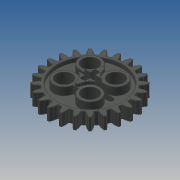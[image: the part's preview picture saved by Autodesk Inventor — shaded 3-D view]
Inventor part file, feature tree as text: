
AUTODESK INVENTOR PART (.ipt)
format: ipt  version: 2022.2 (Build 262287000, 287)  size: 1,320,448 bytes
history: native  units: in
note: dims shown in document units (in); Inventor stores cm internally (conversion verified against a paired STEP export)
features: extrude x5, fillet x2, sketch x1, pattern_circular x1
ambient origin geometry x8: Origin, YZ Plane, XZ Plane, XY Plane, X Axis, Y Axis, Z Axis, Center Point
bodies: Solid1 (feature_tree)
feature tree (9):
  sketch  "Sketch2"  dims[d0=0.189in d2=0.189in d3=0.315in d4=0.315in d5=0.7874in d6=0.8504in d7=0.0551in d8=0.0252in d10=0.9429in d11=1.0205in d12=0.13in d13=0.063in d14=0.063in d15=0.5039in d18=0.3445in d20=0.263in d21=0.0551in d22=0.0in d23=0.1496in d24=0.0in d25=0.2457in d26=0.0in d27=0.0008in d28=0.0008in d29=0.315in d30=0.0in d31=0.1496in d32=0.0in d34=0.0039in d35=9.4488in d36=360.0deg d38=0.0039in]
  extrude  "Extrusion1"  Depth=0.0039in
  extrude  "Extrusion2"  Depth=0.0039in
  extrude  "Extrusion3"  Depth=0.0039in
  extrude  "Extrusion4"  Depth=0.0039in
  extrude  "Extrusion5"  Depth=0.0039in
  fillet  "Fillet2"  Radius=0.0551in
  pattern_circular  "Circular Pattern1"  [2 undecoded]
  fillet  "Fillet3"  Radius=0.9429in
note: 2 required parameter values undecoded (feature->parameter linkage not recoverable at this tier; creation-order binding heuristic only, values carry confidence <= 0.55)
